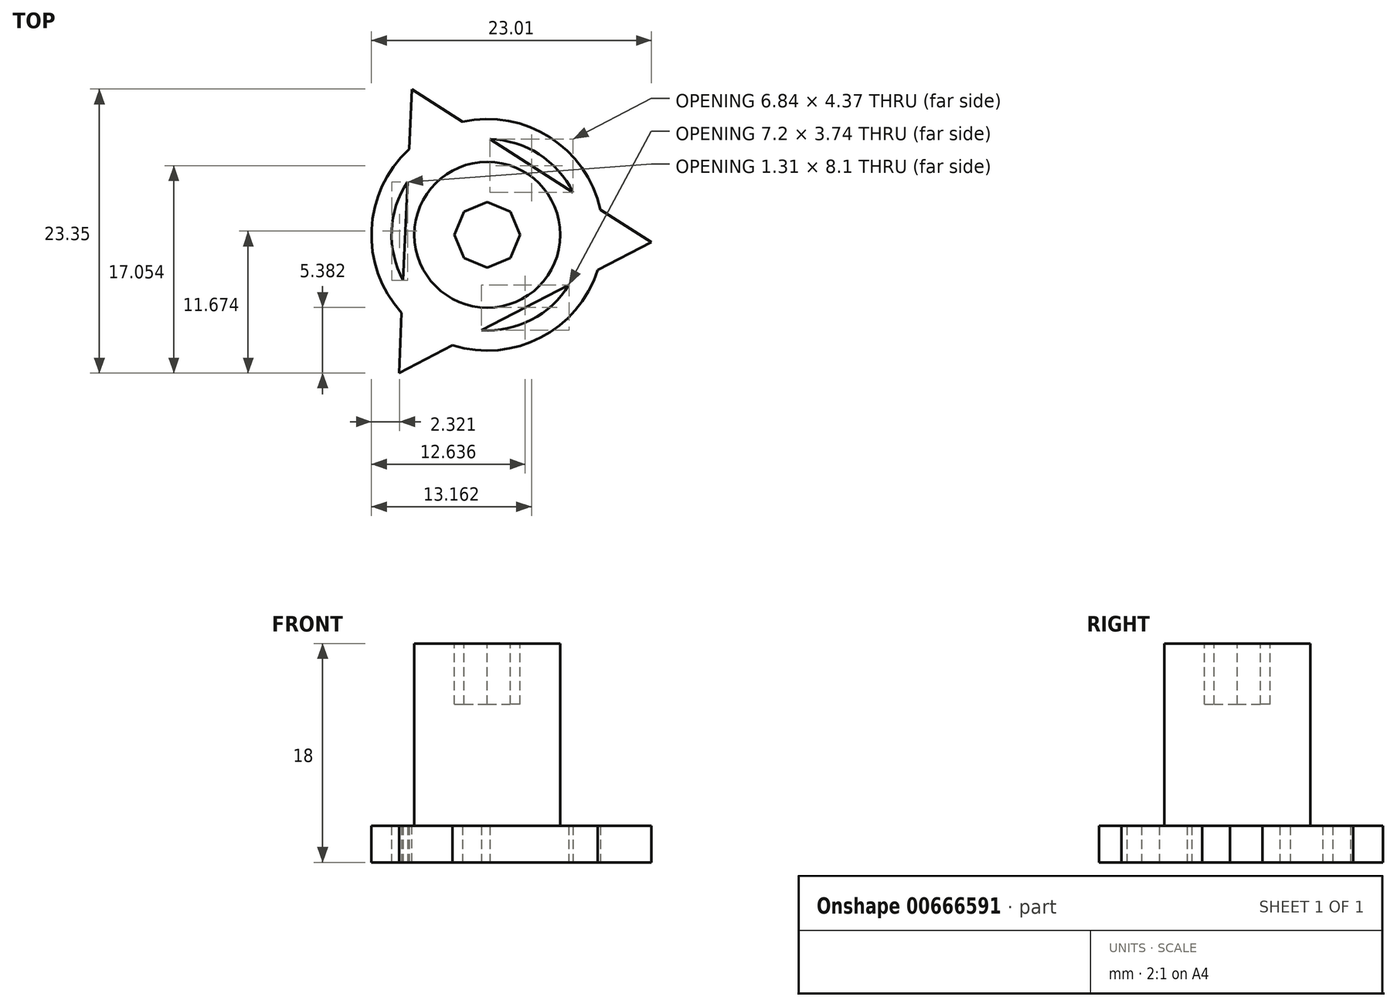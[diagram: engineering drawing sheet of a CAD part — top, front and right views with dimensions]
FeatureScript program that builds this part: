
annotation { "Feature Type Name" : "Feature", "Feature Type Description" : "" }
export const myFeature = defineFeature(function(context is Context, id is Id, definition is map)
    precondition{}
    {
        {
            var Q0;
            Q0=qCreatedBy(makeId("Top.planeOp"),FACE);
            var sketch = newSketch(context, id + "F0", { "sketchPlane" : qUnion([Q0])});
            skCircle(sketch, "E0", {"center": v(0, 0) * mm, "radius": 6 * mm});
            skSolve(sketch);
        }
        {
            var Q0;
            Q0 = qSketchRegion(id + "F0", true);
            extrude(context, id + "F1", {"entities" : qUnion([Q0]), "depth" : 15 * mm, "offsetDistance" : 25 * mm});
        }
        {
            var Q0;
            Q0=makeQuery(id+"F1.opExtrude","CAP_FACE",FACE,{"disambiguationData":[OSD([sQuery(id+"F0.wireOp",EDGE,"E0")])],"isStart":false});
            var sketch = newSketch(context, id + "F2", { "sketchPlane" : qUnion([Q0])});
            skCircle(sketch, "E1.cCircle", {"center": v(0, 0) * mm, "radius": 2.7 * mm, "construction": true});
            skLineSegment(sketch, "E1.0", {"start": v(0, 2.7) * mm, "end": v(1.91, 1.91) * mm});
            skLineSegment(sketch, "E1.1", {"start": v(1.91, 1.91) * mm, "end": v(2.7, 0) * mm});
            skLineSegment(sketch, "E1.2", {"start": v(2.7, 0) * mm, "end": v(1.91, -1.91) * mm});
            skLineSegment(sketch, "E1.3", {"start": v(1.91, -1.91) * mm, "end": v(0, -2.7) * mm});
            skLineSegment(sketch, "E1.4", {"start": v(0, -2.7) * mm, "end": v(-1.91, -1.91) * mm});
            skLineSegment(sketch, "E1.5", {"start": v(-1.91, -1.91) * mm, "end": v(-2.7, 0) * mm});
            skLineSegment(sketch, "E1.6", {"start": v(-2.7, 0) * mm, "end": v(-1.91, 1.91) * mm});
            skLineSegment(sketch, "E1.7", {"start": v(-1.91, 1.91) * mm, "end": v(0, 2.7) * mm});
            skSolve(sketch);
        }
        {
            var Q0;
            Q0=makeQuery(id+"F2.imprint","IMPRINT",FACE,{"disambiguationData":[TD([[makeQuery(id+"F2.imprint","IMPRINT",EDGE,{"derivedFrom":sQuery(id+"F2.wireOp",EDGE,"E1.0")}),-1.0]])]});
            extrude(context, id + "F3", {"entities" : qUnion([Q0]), "operationType" : NewBodyOperationType.REMOVE, "oppositeDirection" : true, "depth" : 5 * mm, "offsetDistance" : 25 * mm});
        }
        {
            var Q0;
            Q0=makeQuery(id+"F1.opExtrude","CAP_FACE",FACE,{"disambiguationData":[OSD([sQuery(id+"F0.wireOp",EDGE,"E0")])],"isStart":true});
            var sketch = newSketch(context, id + "F4", { "sketchPlane" : qUnion([Q0])});
            skCircle(sketch, "E2.cCircle", {"center": v(0, 0) * mm, "radius": 13.5 * mm, "construction": true});
            skLineSegment(sketch, "E2.0", {"start": v(13.48, 0.6) * mm, "end": v(-6.21, -11.98) * mm});
            skLineSegment(sketch, "E2.1", {"start": v(-6.21, -11.98) * mm, "end": v(-7.26, 11.37) * mm});
            skLineSegment(sketch, "E2.2", {"start": v(-7.26, 11.37) * mm, "end": v(13.48, 0.6) * mm});
            skSolve(sketch);
        }
        {
            var Q0;
            Q0 = qSketchRegion(id + "F4", true);
            extrude(context, id + "F5", {"entities" : qUnion([Q0]), "operationType" : NewBodyOperationType.ADD, "depth" : 3 * mm, "offsetDistance" : 25 * mm});
        }
        {
            var Q0;
            Q0=makeQuery(id+"F5.opExtrude","CAP_FACE",FACE,{"disambiguationData":[OSD([sQuery(id+"F4.wireOp",EDGE,"E2.0"),sQuery(id+"F4.wireOp",EDGE,"E2.1"),sQuery(id+"F4.wireOp",EDGE,"E2.2")])],"isStart":false});
            var sketch = newSketch(context, id + "F6", { "sketchPlane" : qUnion([Q0])});
            skCircle(sketch, "E3", {"center": v(0, 0) * mm, "radius": 7.87 * mm});
            skCircle(sketch, "E4", {"center": v(0, 0) * mm, "radius": 9.53 * mm});
            skSolve(sketch);
        }
        {
            var Q0;
            Q0 = qSketchRegion(id + "F6", true);
            extrude(context, id + "F7", {"entities" : qUnion([Q0]), "operationType" : NewBodyOperationType.ADD, "oppositeDirection" : true, "depth" : 3 * mm, "offsetDistance" : 25 * mm});
        }
    });
